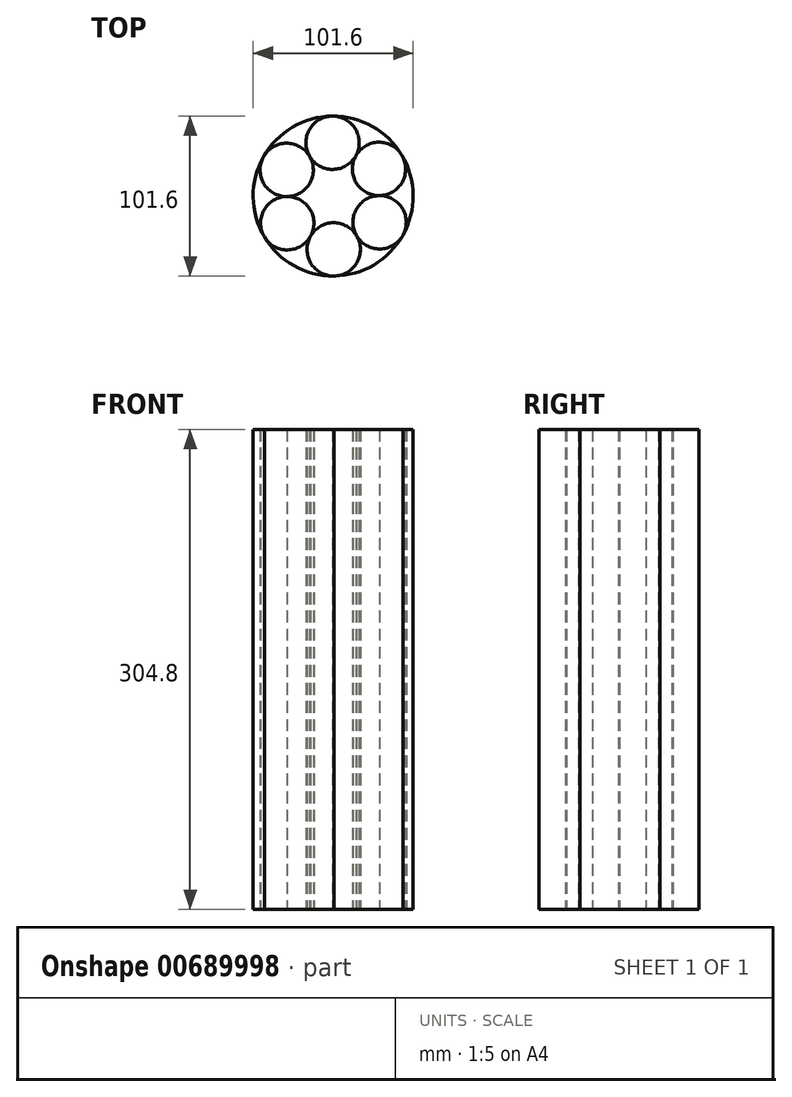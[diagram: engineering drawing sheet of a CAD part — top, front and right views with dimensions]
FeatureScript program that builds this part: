
annotation { "Feature Type Name" : "Feature", "Feature Type Description" : "" }
export const myFeature = defineFeature(function(context is Context, id is Id, definition is map)
    precondition{}
    {
        {
            var Q0;
            Q0=qCreatedBy(makeId("Top.planeOp"),FACE);
            var sketch = newSketch(context, id + "F0", { "sketchPlane" : qUnion([Q0])});
            skCircle(sketch, "E0", {"center": v(0, 0) * mm, "radius": 50.8 * mm});
            skCircle(sketch, "E1.cCircle", {"center": v(0, 0) * mm, "radius": 50.8 * mm, "construction": true});
            skCircle(sketch, "E2", {"center": v(29.5, -16.62) * mm, "radius": 16.93 * mm});
            skCircle(sketch, "E3", {"center": v(0.36, -33.86) * mm, "radius": 16.93 * mm});
            skCircle(sketch, "E4", {"center": v(-29.15, -17.24) * mm, "radius": 16.93 * mm});
            skCircle(sketch, "E5", {"center": v(-29.5, 16.62) * mm, "radius": 16.93 * mm});
            skCircle(sketch, "E6", {"center": v(-0.36, 33.86) * mm, "radius": 16.93 * mm});
            skCircle(sketch, "E7", {"center": v(29.15, 17.24) * mm, "radius": 16.93 * mm});
            skSolve(sketch);
        }
        {
            var Q0;
            {var subQ0=sQuery(id+"F0.wireOp",EDGE,"E4");var subQ1=sQuery(id+"F0.wireOp",EDGE,"E0");var subQ2=makeQuery(id+"F0.imprint","INTERSECT",VERTEX,{"derivedFrom":[subQ1,subQ0]});Q0=makeQuery(id+"F0.imprint","IMPRINT",FACE,{"disambiguationData":[TD([[makeQuery(id+"F0.imprint","IMPRINT",EDGE,{"disambiguationData":[TD([[subQ2,-1.0]])],"derivedFrom":subQ1}),1.0]])]});}
            var Q1;
            {var subQ0=sQuery(id+"F0.wireOp",EDGE,"E5");var subQ1=sQuery(id+"F0.wireOp",EDGE,"E0");var subQ2=makeQuery(id+"F0.imprint","INTERSECT",VERTEX,{"derivedFrom":[subQ1,subQ0]});Q1=makeQuery(id+"F0.imprint","IMPRINT",FACE,{"disambiguationData":[TD([[makeQuery(id+"F0.imprint","IMPRINT",EDGE,{"disambiguationData":[TD([[subQ2,-1.0]])],"derivedFrom":subQ1}),1.0]])]});}
            var Q2;
            {var subQ0=sQuery(id+"F0.wireOp",EDGE,"E6");var subQ1=sQuery(id+"F0.wireOp",EDGE,"E0");var subQ2=makeQuery(id+"F0.imprint","INTERSECT",VERTEX,{"derivedFrom":[subQ1,subQ0]});Q2=makeQuery(id+"F0.imprint","IMPRINT",FACE,{"disambiguationData":[TD([[makeQuery(id+"F0.imprint","IMPRINT",EDGE,{"disambiguationData":[TD([[subQ2,-1.0]])],"derivedFrom":subQ1}),1.0]])]});}
            var Q3;
            {var subQ0=sQuery(id+"F0.wireOp",EDGE,"E6");var subQ1=sQuery(id+"F0.wireOp",EDGE,"E0");var subQ2=makeQuery(id+"F0.imprint","INTERSECT",VERTEX,{"derivedFrom":[subQ1,subQ0]});Q3=makeQuery(id+"F0.imprint","IMPRINT",FACE,{"disambiguationData":[TD([[makeQuery(id+"F0.imprint","IMPRINT",EDGE,{"disambiguationData":[TD([[subQ2,1.0]])],"derivedFrom":subQ1}),1.0]])]});}
            var Q4;
            {var subQ0=sQuery(id+"F0.wireOp",EDGE,"E7");var subQ1=sQuery(id+"F0.wireOp",EDGE,"E0");var subQ2=makeQuery(id+"F0.imprint","INTERSECT",VERTEX,{"derivedFrom":[subQ1,subQ0]});Q4=makeQuery(id+"F0.imprint","IMPRINT",FACE,{"disambiguationData":[TD([[makeQuery(id+"F0.imprint","IMPRINT",EDGE,{"disambiguationData":[TD([[subQ2,1.0]])],"derivedFrom":subQ1}),1.0]])]});}
            var Q5;
            {var subQ0=sQuery(id+"F0.wireOp",EDGE,"E3");var subQ1=sQuery(id+"F0.wireOp",EDGE,"E0");var subQ2=makeQuery(id+"F0.imprint","INTERSECT",VERTEX,{"derivedFrom":[subQ1,subQ0]});Q5=makeQuery(id+"F0.imprint","IMPRINT",FACE,{"disambiguationData":[TD([[makeQuery(id+"F0.imprint","IMPRINT",EDGE,{"disambiguationData":[TD([[subQ2,-1.0]])],"derivedFrom":subQ1}),1.0]])]});}
            var Q6;
            {var subQ5=sQuery(id+"F0.wireOp",EDGE,"E3");var subQ6=sQuery(id+"F0.wireOp",EDGE,"E2");var subQ7=makeQuery(id+"F0.imprint","INTERSECT",VERTEX,{"derivedFrom":[subQ6,subQ5]});Q6=makeQuery(id+"F0.imprint","IMPRINT",FACE,{"disambiguationData":[TD([[makeQuery(id+"F0.imprint","IMPRINT",EDGE,{"disambiguationData":[TD([[subQ7,1.0]])],"derivedFrom":subQ6}),-1.0]])]});}
            extrude(context, id + "F1", {"entities" : qUnion([Q0, Q1, Q2, Q3, Q4, Q5, Q6]), "depth" : 152.4 * mm, "offsetDistance" : 25.4 * mm, "hasSecondDirection" : true, "secondDirectionOppositeDirection" : true, "secondDirectionDepth" : 152.4 * mm});
        }
    });
